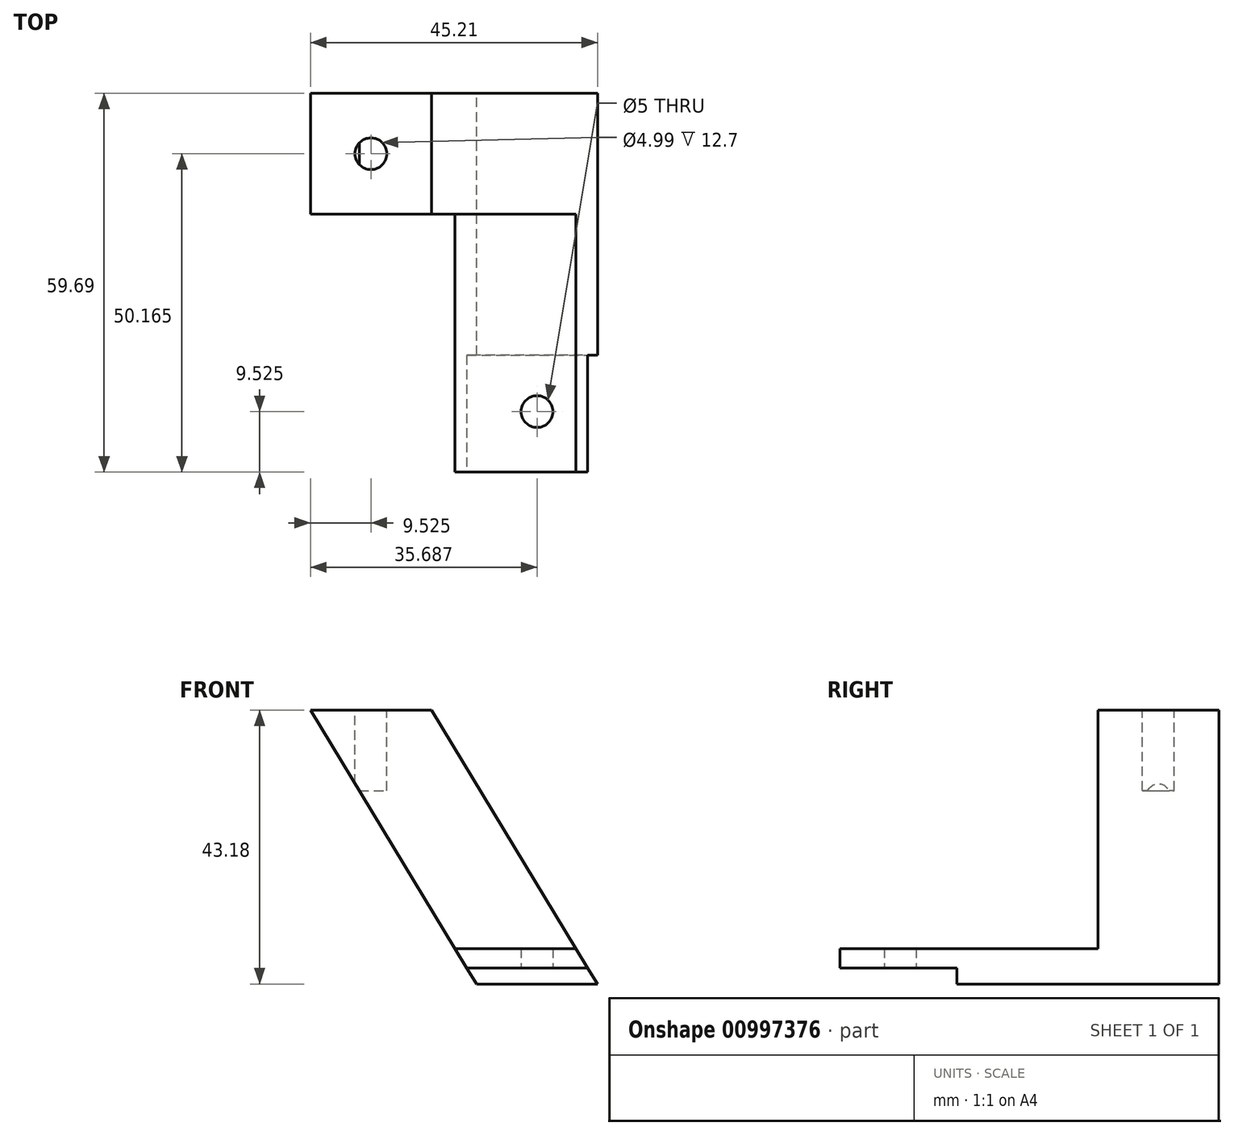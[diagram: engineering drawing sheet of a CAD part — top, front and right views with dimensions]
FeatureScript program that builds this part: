
annotation { "Feature Type Name" : "Feature", "Feature Type Description" : "" }
export const myFeature = defineFeature(function(context is Context, id is Id, definition is map)
    precondition{}
    {
        {
            var Q0;
            Q0=qCreatedBy(makeId("Front.planeOp"),FACE);
            var sketch = newSketch(context, id + "F0", { "sketchPlane" : qUnion([Q0])});
            skLineSegment(sketch, "E0", {"start": v(0, 43.18) * mm, "end": v(19.05, 43.18) * mm});
            skLineSegment(sketch, "E1", {"start": v(35.69, 0) * mm, "end": v(45.21, 0) * mm});
            skLineSegment(sketch, "E2", {"start": v(35.69, 0) * mm, "end": v(26.16, 0) * mm});
            skLineSegment(sketch, "E3", {"start": v(26.16, 0) * mm, "end": v(0, 43.18) * mm});
            skLineSegment(sketch, "E4", {"start": v(19.05, 43.18) * mm, "end": v(45.21, 0) * mm});
            skSolve(sketch);
        }
        {
            var Q0;
            Q0=makeQuery(id+"F0.imprint","IMPRINT",FACE,{"disambiguationData":[TD([[makeQuery(id+"F0.imprint","IMPRINT",EDGE,{"derivedFrom":sQuery(id+"F0.wireOp",EDGE,"E0")}),-1.0]])]});
            extrude(context, id + "F1", {"entities" : qUnion([Q0]), "depth" : 19.05 * mm, "offsetDistance" : 25.4 * mm});
        }
        {
            var Q0;
            Q0=makeQuery(id+"F1.opExtrude","CAP_FACE",FACE,{"disambiguationData":[OSD([sQuery(id+"F0.wireOp",EDGE,"E0"),sQuery(id+"F0.wireOp",EDGE,"E1"),sQuery(id+"F0.wireOp",EDGE,"E2"),sQuery(id+"F0.wireOp",EDGE,"E3"),sQuery(id+"F0.wireOp",EDGE,"E4")])],"isStart":false});
            var sketch = newSketch(context, id + "F2", { "sketchPlane" : qUnion([Q0])});
            skLineSegment(sketch, "E5", {"start": v(22.78, 5.59) * mm, "end": v(41.83, 5.59) * mm});
            skLineSegment(sketch, "E6", {"start": v(41.83, 5.59) * mm, "end": v(45.21, 0) * mm});
            skLineSegment(sketch, "E7", {"start": v(45.21, 0) * mm, "end": v(26.16, 0) * mm});
            skLineSegment(sketch, "E8", {"start": v(26.16, 0) * mm, "end": v(22.78, 5.59) * mm});
            skSolve(sketch);
        }
        {
            var Q0;
            Q0=makeQuery(id+"F2.imprint","IMPRINT",FACE,{"disambiguationData":[TD([[makeQuery(id+"F2.imprint","IMPRINT",EDGE,{"derivedFrom":sQuery(id+"F2.wireOp",EDGE,"E5")}),-1.0]])]});
            extrude(context, id + "F3", {"entities" : qUnion([Q0]), "operationType" : NewBodyOperationType.ADD, "depth" : 40.64 * mm, "offsetDistance" : 25.4 * mm});
        }
        {
            var Q0;
            Q0=makeQuery(id+"F1.opExtrude","SWEPT_FACE",FACE,{"disambiguationData":[OSD([sQuery(id+"F0.wireOp",EDGE,"E0")])]});
            var sketch = newSketch(context, id + "F4", { "sketchPlane" : qUnion([Q0])});
            skCircle(sketch, "E9", {"center": v(9.53, -9.53) * mm, "radius": 2.5 * mm});
            skPoint(sketch, "E9.centerSnap0", {"position": v(19.05, -9.53) * mm});
            skPoint(sketch, "E9.centerSnap1", {"position": v(9.53, 0) * mm});
            skSolve(sketch);
        }
        {
            var Q0;
            Q0=makeQuery(id+"F4.imprint","IMPRINT",FACE,{"disambiguationData":[TD([[makeQuery(id+"F4.imprint","IMPRINT",EDGE,{"derivedFrom":sQuery(id+"F4.wireOp",EDGE,"E9")}),1.0]])]});
            extrude(context, id + "F5", {"entities" : qUnion([Q0]), "operationType" : NewBodyOperationType.REMOVE, "oppositeDirection" : true, "depth" : 12.7 * mm, "offsetDistance" : 25.4 * mm});
        }
        {
            var Q0;
            Q0=makeQuery(id+"F3.boolean.opBoolean","MERGE",FACE,{"derivedFrom":[makeQuery(id+"F1.opExtrude","SWEPT_FACE",FACE,{"disambiguationData":[OSD([sQuery(id+"F0.wireOp",EDGE,"E1"),sQuery(id+"F0.wireOp",EDGE,"E2")])]}),makeQuery(id+"F3.opExtrude","SWEPT_FACE",FACE,{"disambiguationData":[OSD([sQuery(id+"F2.wireOp",EDGE,"E7")])]})]});
            var sketch = newSketch(context, id + "F6", { "sketchPlane" : qUnion([Q0])});
            skLineSegment(sketch, "E10", {"start": v(35.69, 59.7) * mm, "end": v(35.69, 50.17) * mm});
            skCircle(sketch, "E11", {"center": v(35.69, 50.17) * mm, "radius": 2.5 * mm});
            skSolve(sketch);
        }
        {
            var Q0;
            Q0=makeQuery(id+"F6.imprint","IMPRINT",FACE,{"disambiguationData":[TD([[makeQuery(id+"F6.imprint","IMPRINT",EDGE,{"derivedFrom":sQuery(id+"F6.wireOp",EDGE,"E11")}),1.0]])]});
            extrude(context, id + "F7", {"entities" : qUnion([Q0]), "operationType" : NewBodyOperationType.REMOVE, "endBound" : BoundingType.THROUGH_ALL, "oppositeDirection" : true, "depth" : 25.4 * mm, "offsetDistance" : 25.4 * mm});
        }
        {
            var Q0;
            Q0=makeQuery(id+"F3.opExtrude","CAP_FACE",FACE,{"disambiguationData":[OSD([sQuery(id+"F2.wireOp",EDGE,"E5"),sQuery(id+"F2.wireOp",EDGE,"E6"),sQuery(id+"F2.wireOp",EDGE,"E7"),sQuery(id+"F2.wireOp",EDGE,"E8")])],"isStart":false});
            var sketch = newSketch(context, id + "F8", { "sketchPlane" : qUnion([Q0])});
            skLineSegment(sketch, "E12", {"start": v(24.62, 2.54) * mm, "end": v(43.67, 2.54) * mm});
            skLineSegment(sketch, "E13", {"start": v(43.67, 2.54) * mm, "end": v(45.21, 0) * mm});
            skLineSegment(sketch, "E14", {"start": v(45.21, 0) * mm, "end": v(26.16, 0) * mm});
            skLineSegment(sketch, "E15", {"start": v(26.16, 0) * mm, "end": v(24.62, 2.54) * mm});
            skSolve(sketch);
        }
        {
            var Q0;
            Q0=makeQuery(id+"F8.imprint","IMPRINT",FACE,{"disambiguationData":[TD([[makeQuery(id+"F8.imprint","IMPRINT",EDGE,{"derivedFrom":sQuery(id+"F8.wireOp",EDGE,"E12")}),-1.0]])]});
            extrude(context, id + "F9", {"entities" : qUnion([Q0]), "operationType" : NewBodyOperationType.REMOVE, "oppositeDirection" : true, "depth" : 18.41 * mm, "offsetDistance" : 25.4 * mm});
        }
    });
